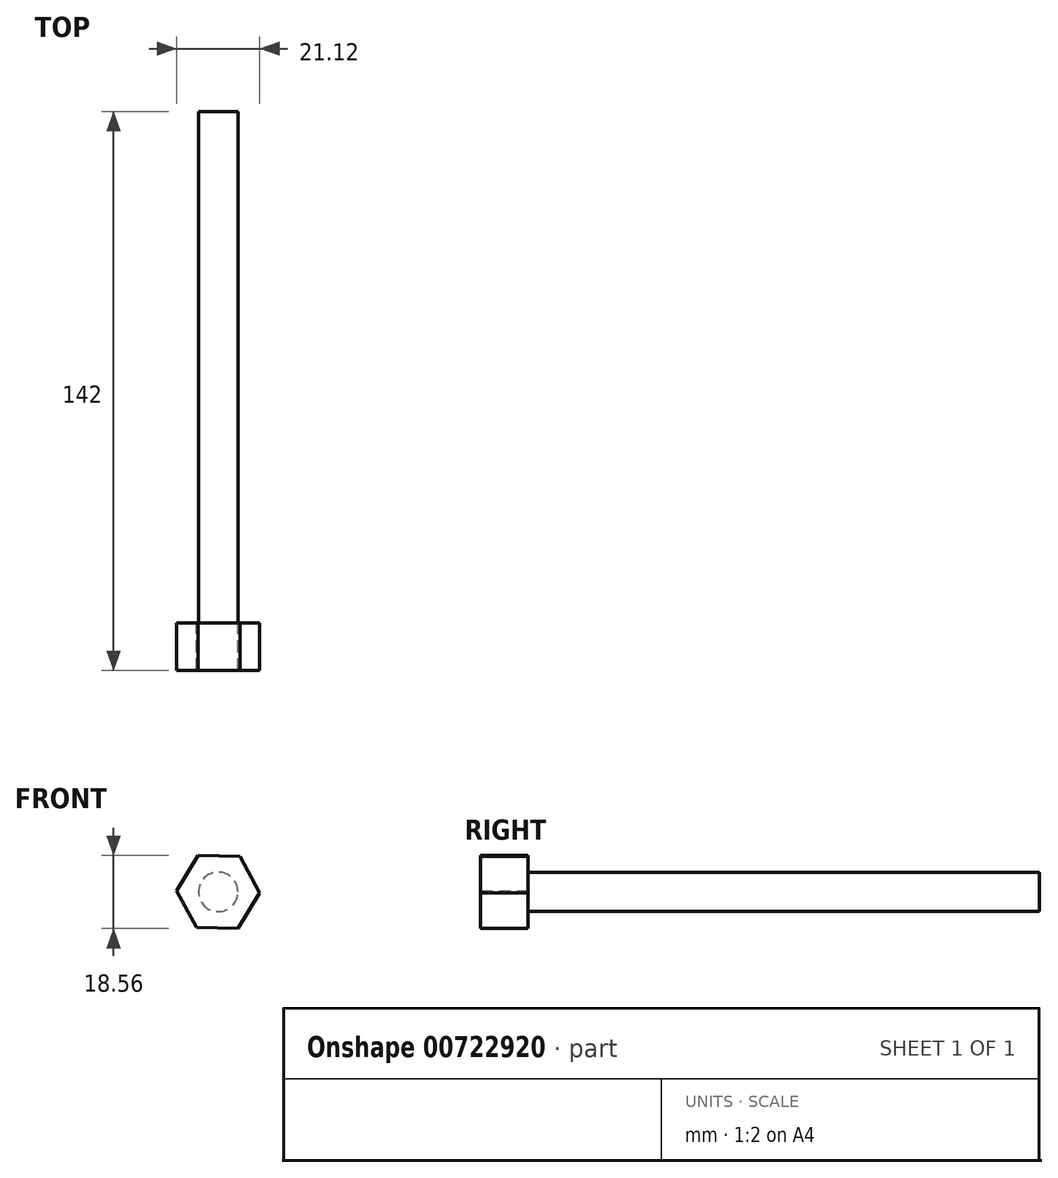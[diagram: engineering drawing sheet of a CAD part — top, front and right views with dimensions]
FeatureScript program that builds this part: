
annotation { "Feature Type Name" : "Feature", "Feature Type Description" : "" }
export const myFeature = defineFeature(function(context is Context, id is Id, definition is map)
    precondition{}
    {
        {
            var Q0;
            Q0=qCreatedBy(makeId("Front.planeOp"),FACE);
            var sketch = newSketch(context, id + "F0", { "sketchPlane" : qUnion([Q0])});
            skCircle(sketch, "E0", {"center": v(0, 0) * mm, "radius": 5 * mm});
            skSolve(sketch);
        }
        {
            var Q0;
            Q0 = qSketchRegion(id + "F0", true);
            extrude(context, id + "F1", {"entities" : qUnion([Q0]), "depth" : 130 * mm, "offsetDistance" : 25 * mm});
        }
        {
            var Q0;
            Q0=makeQuery(id+"F1.opExtrude","CAP_FACE",FACE,{"disambiguationData":[OSD([sQuery(id+"F0.wireOp",EDGE,"E0")])],"isStart":false});
            var sketch = newSketch(context, id + "F2", { "sketchPlane" : qUnion([Q0])});
            skCircle(sketch, "E1.cCircle", {"center": v(0, 0) * mm, "radius": 9.15 * mm, "construction": true});
            skLineSegment(sketch, "E1.0", {"start": v(5.51, 9.01) * mm, "end": v(10.56, -0.27) * mm});
            skLineSegment(sketch, "E1.1", {"start": v(10.56, -0.27) * mm, "end": v(5.05, -9.28) * mm});
            skLineSegment(sketch, "E1.2", {"start": v(5.05, -9.28) * mm, "end": v(-5.51, -9.01) * mm});
            skLineSegment(sketch, "E1.3", {"start": v(-5.51, -9.01) * mm, "end": v(-10.56, 0.27) * mm});
            skLineSegment(sketch, "E1.4", {"start": v(-10.56, 0.27) * mm, "end": v(-5.05, 9.28) * mm});
            skLineSegment(sketch, "E1.5", {"start": v(-5.05, 9.28) * mm, "end": v(5.51, 9.01) * mm});
            skPoint(sketch, "E1.0.midPoint", {"position": v(8.04, 4.37) * mm});
            skSolve(sketch);
        }
        {
            var Q0;
            Q0=makeQuery(id+"F2.imprint","IMPRINT",FACE,{"disambiguationData":[TD([[makeQuery(id+"F2.imprint","IMPRINT",EDGE,{"derivedFrom":sQuery(id+"F2.wireOp",EDGE,"E1.0")}),-1.0]])]});
            var Q1;
            Q1=makeQuery(id+"F2.imprint","IMPRINT",FACE,{"disambiguationData":[TD([[makeQuery(id+"F2.imprint","IMPRINT",EDGE,{"derivedFrom":makeQuery(id+"F1.opExtrude","CAP_EDGE",EDGE,{"disambiguationData":[OSD([sQuery(id+"F0.wireOp",EDGE,"E0")])],"isStart":false})}),1.0]])]});
            extrude(context, id + "F3", {"entities" : qUnion([Q0, Q1]), "operationType" : NewBodyOperationType.ADD, "depth" : 12 * mm, "offsetDistance" : 25 * mm});
        }
    });
